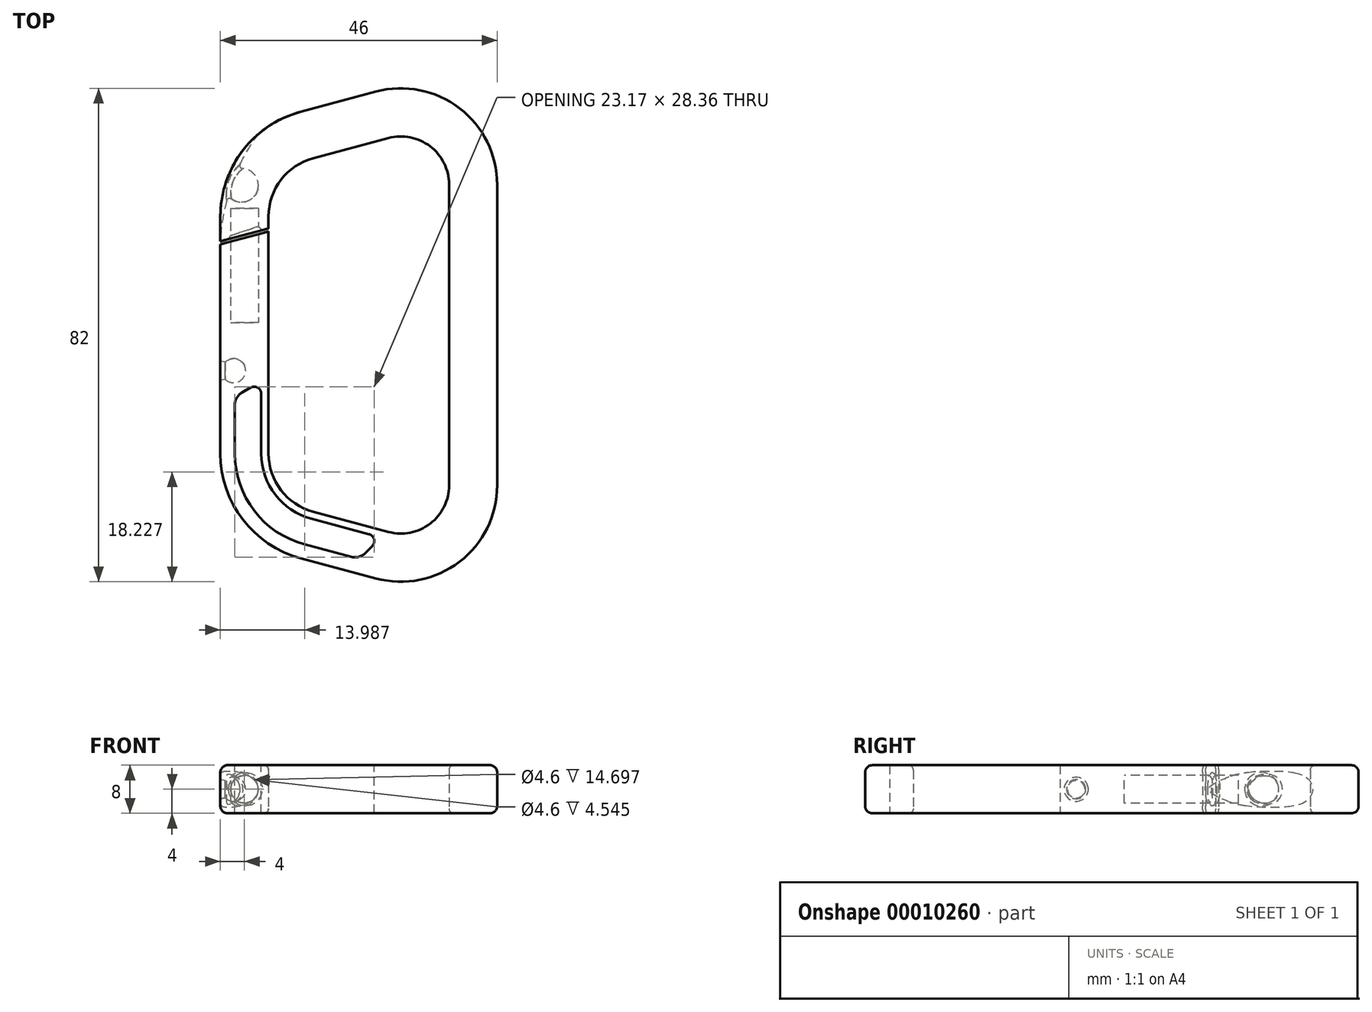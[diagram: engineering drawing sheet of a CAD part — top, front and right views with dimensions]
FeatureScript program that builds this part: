
annotation { "Feature Type Name" : "Feature", "Feature Type Description" : "" }
export const myFeature = defineFeature(function(context is Context, id is Id, definition is map)
    precondition{}
    {
        {
            var Q0;
            Q0=qCreatedBy(makeId("Top.planeOp"),FACE);
            var sketch = newSketch(context, id + "F0", { "sketchPlane" : qUnion([Q0])});
            skLineSegment(sketch, "E0", {"start": v(0, 25) * mm, "end": v(0, -25) * mm});
            skLineSegment(sketch, "E1", {"start": v(-10.07, -32.73) * mm, "end": v(-22.59, -29.37) * mm});
            skLineSegment(sketch, "E2", {"start": v(-22.59, 29.37) * mm, "end": v(-10.07, 32.73) * mm});
            skPoint(sketch, "E3.visualSharp", {"position": v(0, 35.43) * mm});
            skArc(sketch, "E3.filletArc", {"start": v(0, 25) * mm, "mid": v(-3.13, 31.35) * mm, "end": v(-10.07, 32.73) * mm});
            skPoint(sketch, "E4.visualSharp", {"position": v(0, -35.43) * mm});
            skArc(sketch, "E4.filletArc", {"start": v(-10.07, -32.73) * mm, "mid": v(-3.13, -31.35) * mm, "end": v(0, -25) * mm});
            skLineSegment(sketch, "E5", {"start": v(-30, 19.71) * mm, "end": v(-30, 17.71) * mm});
            skLineSegment(sketch, "E6", {"start": v(-30, -19.71) * mm, "end": v(-30, 17.21) * mm});
            skPoint(sketch, "E7.visualSharp", {"position": v(-30, -27.39) * mm});
            skArc(sketch, "E7.filletArc", {"start": v(-30, -19.71) * mm, "mid": v(-27.93, -25.8) * mm, "end": v(-22.59, -29.37) * mm});
            skPoint(sketch, "E8.visualSharp", {"position": v(-30, 27.39) * mm});
            skArc(sketch, "E8.filletArc", {"start": v(-22.59, 29.37) * mm, "mid": v(-27.93, 25.8) * mm, "end": v(-30, 19.71) * mm});
            skLineSegment(sketch, "E9.0", {"start": v(-38, -19.71) * mm, "end": v(-38, 15.07) * mm});
            skArc(sketch, "E9.1", {"start": v(-38, -19.71) * mm, "mid": v(-34.28, -30.67) * mm, "end": v(-24.66, -37.1) * mm});
            skLineSegment(sketch, "E9.2", {"start": v(-12.14, -40.45) * mm, "end": v(-24.66, -37.1) * mm});
            skArc(sketch, "E9.3", {"start": v(-12.14, -40.45) * mm, "mid": v(1.74, -37.7) * mm, "end": v(8, -25) * mm});
            skLineSegment(sketch, "E9.4", {"start": v(8, 25) * mm, "end": v(8, -25) * mm});
            skArc(sketch, "E9.5", {"start": v(8, 25) * mm, "mid": v(1.74, 37.7) * mm, "end": v(-12.14, 40.45) * mm});
            skLineSegment(sketch, "E9.6", {"start": v(-24.66, 37.1) * mm, "end": v(-12.14, 40.45) * mm});
            skArc(sketch, "E9.7", {"start": v(-24.66, 37.1) * mm, "mid": v(-34.28, 30.67) * mm, "end": v(-38, 19.71) * mm});
            skLineSegment(sketch, "E9.8", {"start": v(-38, 19.71) * mm, "end": v(-38, 15.57) * mm});
            skLineSegment(sketch, "E10", {"start": v(-38, 15.57) * mm, "end": v(-30, 17.71) * mm});
            skLineSegment(sketch, "E11", {"start": v(-38, 15.07) * mm, "end": v(-30, 17.21) * mm});
            skLineSegment(sketch, "E12", {"start": v(-30, 17.21) * mm, "end": v(-30, 17.71) * mm, "construction": true});
            skSolve(sketch);
        }
        {
            var Q0;
            Q0 = qSketchRegion(id + "F0", true);
            extrude(context, id + "F1", {"entities" : qUnion([Q0]), "endBound" : BoundingType.SYMMETRIC, "depth" : 8 * mm});
        }
        {
            var Q0;
            Q0=qCreatedBy(makeId("Front.planeOp"),FACE);
            var Q1;
            Q1=makeQuery(id+"F1.opExtrude","CAP_VERTEX",VERTEX,{"disambiguationData":[OSD([sQuery(id+"F0.wireOp",EDGE,"E9.0"),sQuery(id+"F0.wireOp",EDGE,"E11")])],"isStart":false});
            cPlane(context, id + "F2", {"entities" : qUnion([Q0, Q1]), "cplaneType" : CPlaneType.PLANE_POINT, "offset" : 150 * mm, "width" : 150 * mm, "height" : 150 * mm});
        }
        {
            var Q0;
            Q0=qCreatedBy(id+"F2.planeOp",FACE);
            var sketch = newSketch(context, id + "F3", { "sketchPlane" : qUnion([Q0])});
            skCircle(sketch, "E13", {"center": v(-34, 0) * mm, "radius": 2.3 * mm});
            skLineSegment(sketch, "E14", {"start": v(-38, 4) * mm, "end": v(-30, -4) * mm, "construction": true});
            skSolve(sketch);
        }
        {
            var Q0;
            Q0 = qSketchRegion(id + "F3", true);
            extrude(context, id + "F4", {"entities" : qUnion([Q0]), "operationType" : NewBodyOperationType.REMOVE, "oppositeDirection" : true, "depth" : 6 * mm, "hasSecondDirection" : true, "secondDirectionOppositeDirection" : false, "secondDirectionDepth" : 13 * mm});
        }
        {
            var Q0;
            Q0=qCreatedBy(makeId("Top.planeOp"),FACE);
            var sketch = newSketch(context, id + "F5", { "sketchPlane" : qUnion([Q0])});
            skCircle(sketch, "E15", {"center": v(-34.5, 24.87) * mm, "radius": 2.8 * mm, "construction": true});
            skLineSegment(sketch, "E16", {"start": v(-34.5, 24.87) * mm, "end": v(-38, 24.87) * mm, "construction": true});
            skArc(sketch, "E17", {"start": v(-37.23, 25.47) * mm, "mid": v(-35.1, 22.14) * mm, "end": v(-31.77, 24.27) * mm});
            skLineSegment(sketch, "E18", {"start": v(-31.77, 24.27) * mm, "end": v(-37.23, 25.47) * mm});
            skLineSegment(sketch, "E19", {"start": v(-38.17, 20.9) * mm, "end": v(-36.12, 30.17) * mm, "construction": true});
            skLineSegment(sketch, "E20", {"start": v(-37.26, 22.07) * mm, "end": v(-34.5, 22.07) * mm, "construction": true});
            skSolve(sketch);
        }
        {
            var Q0;
            Q0=makeQuery(id+"F5.imprint","IMPRINT",FACE,{"disambiguationData":[TD([[makeQuery(id+"F5.imprint","IMPRINT",EDGE,{"derivedFrom":sQuery(id+"F5.wireOp",EDGE,"E17")}),1.0]])]});
            var Q1;
            Q1=sQuery(id+"F5.wireOp",EDGE,"E18");
            revolve(context, id + "F6", {"operationType" : NewBodyOperationType.REMOVE, "entities" : qUnion([Q0]), "axis" : qUnion([Q1]), "revolveType" : RevolveType.FULL, "oppositeDirection" : true});
        }
        {
            var Q0;
            Q0=qCreatedBy(makeId("Top.planeOp"),FACE);
            var sketch = newSketch(context, id + "F7", { "sketchPlane" : qUnion([Q0])});
            skLineSegment(sketch, "E21", {"start": v(-37.02, 37.41) * mm, "end": v(-44.4, 16.69) * mm});
            skLineSegment(sketch, "E22", {"start": v(-36.56, 26.77) * mm, "end": v(-37.3, 24.7) * mm, "construction": true});
            skLineSegment(sketch, "E23", {"start": v(-36.93, 25.73) * mm, "end": v(-35.99, 25.4) * mm, "construction": true});
            skLineSegment(sketch, "E24", {"start": v(-37.02, 37.41) * mm, "end": v(-30.42, 35.07) * mm});
            skLineSegment(sketch, "E25", {"start": v(-44.4, 16.69) * mm, "end": v(-38.08, 14.44) * mm});
            skArc(sketch, "E26", {"start": v(-30.42, 35.07) * mm, "mid": v(-35.99, 25.4) * mm, "end": v(-38.08, 14.44) * mm});
            skSolve(sketch);
        }
        {
            var Q0;
            Q0 = qSketchRegion(id + "F7", true);
            var Q1;
            Q1=sQuery(id+"F7.wireOp",EDGE,"E21");
            revolve(context, id + "F8", {"operationType" : NewBodyOperationType.REMOVE, "entities" : qUnion([Q0]), "axis" : qUnion([Q1]), "revolveType" : RevolveType.FULL, "oppositeDirection" : true});
        }
        {
            var Q0;
            Q0=makeQuery(id+"F8.boolean.opBoolean","INTERSECT",EDGE,{"derivedFrom":[makeQuery(id+"F6.boolean.opBoolean","COPY",FACE,{"derivedFrom":makeQuery(id+"F6.opRevolve","SWEPT_FACE",FACE,{"disambiguationData":[OSD([sQuery(id+"F5.wireOp",EDGE,"E17")])]})}),makeQuery(id+"F8.opRevolve","SWEPT_FACE",FACE,{"disambiguationData":[OSD([sQuery(id+"F7.wireOp",EDGE,"E26")])]})]});
            fillet(context, id + "F9", {"entities" : qUnion([Q0]), "radius" : .5 * mm, "tangentPropagation" : true, "rho" : .4, "crossSection" : FilletCrossSection.CONIC, "allowEdgeOverflow" : false});
        }
        {
            var Q0;
            Q0=qCreatedBy(makeId("Top.planeOp"),FACE);
            var sketch = newSketch(context, id + "F10", { "sketchPlane" : qUnion([Q0])});
            skLineSegment(sketch, "E27", {"start": v(-38, -4.33) * mm, "end": v(-38, -5.93) * mm});
            skLineSegment(sketch, "E28", {"start": v(-38, -5.93) * mm, "end": v(-33.8, -5.93) * mm});
            skLineSegment(sketch, "E29", {"start": v(-38, -4.33) * mm, "end": v(-37.18, -4.48) * mm});
            skArc(sketch, "E30", {"start": v(-33.8, -5.93) * mm, "mid": v(-35.01, -4.1) * mm, "end": v(-37.18, -4.48) * mm});
            skLineSegment(sketch, "E31", {"start": v(-37.8, -5.93) * mm, "end": v(-37.8, -4.14) * mm, "construction": true});
            skSolve(sketch);
        }
        {
            var Q0;
            Q0 = qSketchRegion(id + "F10", true);
            var Q1;
            Q1=sQuery(id+"F10.wireOp",EDGE,"E28");
            revolve(context, id + "F11", {"operationType" : NewBodyOperationType.REMOVE, "entities" : qUnion([Q0]), "axis" : qUnion([Q1]), "revolveType" : RevolveType.FULL, "oppositeDirection" : true});
        }
        {
            var Q0;
            Q0=makeQuery(id+"F1.opExtrude","CAP_FACE",FACE,{"disambiguationData":[OSD([sQuery(id+"F0.wireOp",EDGE,"E0"),sQuery(id+"F0.wireOp",EDGE,"E1"),sQuery(id+"F0.wireOp",EDGE,"E2"),sQuery(id+"F0.wireOp",EDGE,"E3.filletArc"),sQuery(id+"F0.wireOp",EDGE,"E4.filletArc"),sQuery(id+"F0.wireOp",EDGE,"E5"),sQuery(id+"F0.wireOp",EDGE,"E6"),sQuery(id+"F0.wireOp",EDGE,"E7.filletArc"),sQuery(id+"F0.wireOp",EDGE,"E8.filletArc"),sQuery(id+"F0.wireOp",EDGE,"E9.0"),sQuery(id+"F0.wireOp",EDGE,"E9.1"),sQuery(id+"F0.wireOp",EDGE,"E9.2"),sQuery(id+"F0.wireOp",EDGE,"E9.3"),sQuery(id+"F0.wireOp",EDGE,"E9.4"),sQuery(id+"F0.wireOp",EDGE,"E9.5"),sQuery(id+"F0.wireOp",EDGE,"E9.6"),sQuery(id+"F0.wireOp",EDGE,"E9.7"),sQuery(id+"F0.wireOp",EDGE,"E9.8"),sQuery(id+"F0.wireOp",EDGE,"E10"),sQuery(id+"F0.wireOp",EDGE,"E11")])],"isStart":false});
            var sketch = newSketch(context, id + "F12", { "sketchPlane" : qUnion([Q0])});
            skLineSegment(sketch, "E32.0", {"start": v(-14.9, -37.23) * mm, "end": v(-24.04, -34.78) * mm});
            skArc(sketch, "E32.1", {"start": v(-35.6, -19.71) * mm, "mid": v(-32.38, -29.21) * mm, "end": v(-24.04, -34.78) * mm});
            skLineSegment(sketch, "E32.2", {"start": v(-35.6, -19.71) * mm, "end": v(-35.6, -10.25) * mm});
            skLineSegment(sketch, "E33.0", {"start": v(-11.3, -33.64) * mm, "end": v(-22.9, -30.53) * mm});
            skArc(sketch, "E33.1", {"start": v(-31.2, -19.71) * mm, "mid": v(-28.89, -26.53) * mm, "end": v(-22.9, -30.53) * mm});
            skLineSegment(sketch, "E33.2", {"start": v(-31.2, -19.71) * mm, "end": v(-31.2, -7.71) * mm});
            skLineSegment(sketch, "E34", {"start": v(-31.2, -7.71) * mm, "end": v(-35.6, -10.25) * mm});
            skLineSegment(sketch, "E35", {"start": v(-11.3, -33.64) * mm, "end": v(-14.9, -37.23) * mm});
            skSolve(sketch);
        }
        {
            var Q0;
            Q0 = qSketchRegion(id + "F12", true);
            extrude(context, id + "F13", {"entities" : qUnion([Q0]), "operationType" : NewBodyOperationType.REMOVE, "endBound" : BoundingType.THROUGH_ALL, "oppositeDirection" : true, "depth" : 25 * mm});
        }
        {
            var Q0;
            Q0=makeQuery(id+"F13.boolean.opBoolean","COPY",EDGE,{"derivedFrom":makeQuery(id+"F13.opExtrude","SWEPT_EDGE",EDGE,{"disambiguationData":[OSD([sQuery(id+"F12.wireOp",EDGE,"E32.2"),sQuery(id+"F12.wireOp",EDGE,"E34")])]})});
            var Q1;
            Q1=makeQuery(id+"F13.boolean.opBoolean","COPY",EDGE,{"derivedFrom":makeQuery(id+"F13.opExtrude","SWEPT_EDGE",EDGE,{"disambiguationData":[OSD([sQuery(id+"F12.wireOp",EDGE,"E32.0"),sQuery(id+"F12.wireOp",EDGE,"E35")])]})});
            fillet(context, id + "F14", {"entities" : qUnion([Q0, Q1]), "radius" : 2.4 * mm, "tangentPropagation" : true, "allowEdgeOverflow" : false});
        }
        {
            var Q0;
            Q0=makeQuery(id+"F13.boolean.opBoolean","COPY",EDGE,{"derivedFrom":makeQuery(id+"F13.opExtrude","SWEPT_EDGE",EDGE,{"disambiguationData":[OSD([sQuery(id+"F12.wireOp",EDGE,"E33.2"),sQuery(id+"F12.wireOp",EDGE,"E34")])]})});
            var Q1;
            Q1=makeQuery(id+"F13.boolean.opBoolean","COPY",EDGE,{"derivedFrom":makeQuery(id+"F13.opExtrude","SWEPT_EDGE",EDGE,{"disambiguationData":[OSD([sQuery(id+"F12.wireOp",EDGE,"E33.0"),sQuery(id+"F12.wireOp",EDGE,"E35")])]})});
            fillet(context, id + "F15", {"entities" : qUnion([Q0, Q1]), "radius" : 1.2 * mm, "tangentPropagation" : true, "allowEdgeOverflow" : false});
        }
        {
            var Q0;
            Q0=makeQuery(id+"F1.opExtrude","CAP_EDGE",EDGE,{"disambiguationData":[OSD([sQuery(id+"F0.wireOp",EDGE,"E0")])],"isStart":true});
            var Q1;
            Q1=makeQuery(id+"F1.opExtrude","CAP_EDGE",EDGE,{"disambiguationData":[OSD([sQuery(id+"F0.wireOp",EDGE,"E0")])],"isStart":false});
            fillet(context, id + "F16", {"entities" : qUnion([Q0, Q1]), "radius" : .8 * mm, "tangentPropagation" : true, "allowEdgeOverflow" : false});
        }
        {
            var Q0;
            Q0=makeQuery(id+"F1.opExtrude","CAP_EDGE",EDGE,{"disambiguationData":[OSD([sQuery(id+"F0.wireOp",EDGE,"E9.4")])],"isStart":true});
            var Q1;
            Q1=makeQuery(id+"F1.opExtrude","CAP_EDGE",EDGE,{"disambiguationData":[OSD([sQuery(id+"F0.wireOp",EDGE,"E9.4")])],"isStart":false});
            fillet(context, id + "F17", {"entities" : qUnion([Q0, Q1]), "radius" : 1.2 * mm, "tangentPropagation" : true, "allowEdgeOverflow" : false});
        }
        {
            var Q0;
            Q0=makeQuery(id+"F4.boolean.opBoolean","INTERSECT",EDGE,{"derivedFrom":[makeQuery(id+"F1.opExtrude","SWEPT_FACE",FACE,{"disambiguationData":[OSD([sQuery(id+"F0.wireOp",EDGE,"E10")])]}),makeQuery(id+"F4.opExtrude","SWEPT_FACE",FACE,{"disambiguationData":[OSD([sQuery(id+"F3.wireOp",EDGE,"E13")])]})]});
            chamfer(context, id + "F18", {"entities" : qUnion([Q0]), "chamferType" : ChamferType.OFFSET_ANGLE, "width" : .5 * mm, "oppositeDirection" : true, "angle" : 30 * degree, "tangentPropagation" : true});
        }
    });
